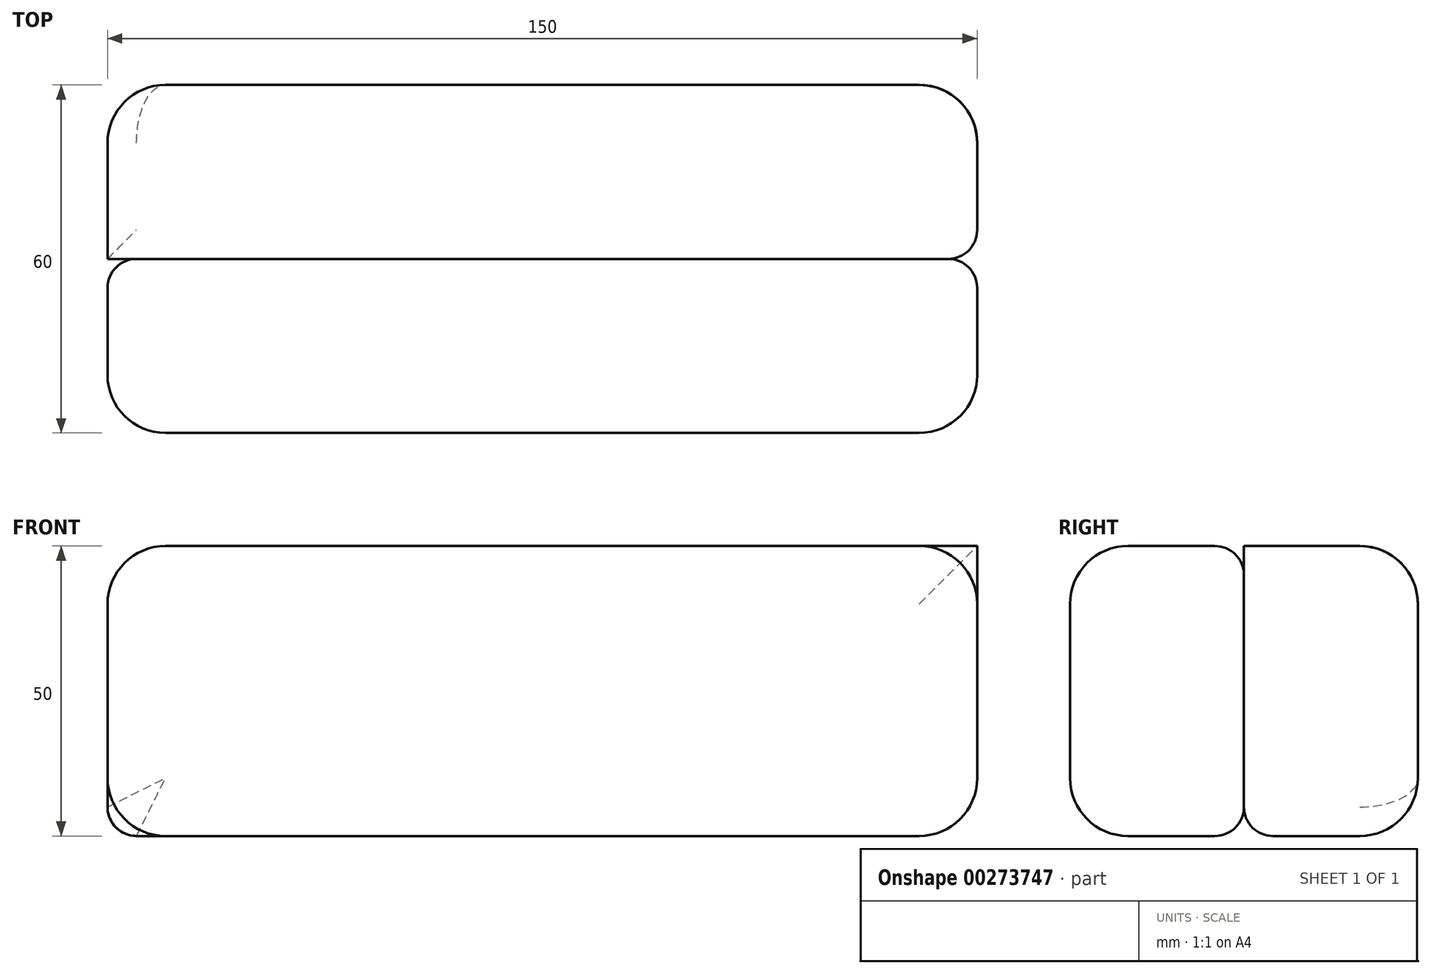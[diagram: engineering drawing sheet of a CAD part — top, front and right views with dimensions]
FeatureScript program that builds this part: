
annotation { "Feature Type Name" : "Feature", "Feature Type Description" : "" }
export const myFeature = defineFeature(function(context is Context, id is Id, definition is map)
    precondition{}
    {
        {
            var Q0;
            Q0=qCreatedBy(makeId("Front.planeOp"),FACE);
            var sketch = newSketch(context, id + "F0", { "sketchPlane" : qUnion([Q0])});
            skLineSegment(sketch, "E0", {"start": v(-86.56, 32.78) * mm, "end": v(-86.56, -17.22) * mm});
            skLineSegment(sketch, "E1", {"start": v(-86.56, -17.22) * mm, "end": v(63.44, -17.22) * mm});
            skLineSegment(sketch, "E2", {"start": v(63.44, -17.22) * mm, "end": v(63.44, 32.78) * mm});
            skLineSegment(sketch, "E3", {"start": v(63.44, 32.78) * mm, "end": v(-86.56, 32.78) * mm});
            skSolve(sketch);
        }
        {
            var Q0;
            Q0=makeQuery(id+"F0.imprint","IMPRINT",FACE,{"disambiguationData":[TD([[makeQuery(id+"F0.imprint","IMPRINT",EDGE,{"derivedFrom":sQuery(id+"F0.wireOp",EDGE,"E0")}),1.0]])]});
            extrude(context, id + "F1", {"entities" : qUnion([Q0]), "depth" : 30 * mm});
        }
        {
            var Q0;
            Q0=makeQuery(id+"F1.opExtrude","CAP_EDGE",EDGE,{"disambiguationData":[OSD([sQuery(id+"F0.wireOp",EDGE,"E3")])],"isStart":false});
            var Q1;
            Q1=makeQuery(id+"F1.opExtrude","CAP_EDGE",EDGE,{"disambiguationData":[OSD([sQuery(id+"F0.wireOp",EDGE,"E1")])],"isStart":false});
            fillet(context, id + "F2", {"entities" : qUnion([Q0, Q1]), "radius" : 10 * mm, "tangentPropagation" : true, "allowEdgeOverflow" : false});
        }
        {
            var Q0;
            Q0=makeQuery(id+"F1.opExtrude","CAP_FACE",FACE,{"disambiguationData":[OSD([sQuery(id+"F0.wireOp",EDGE,"E0"),sQuery(id+"F0.wireOp",EDGE,"E1"),sQuery(id+"F0.wireOp",EDGE,"E2"),sQuery(id+"F0.wireOp",EDGE,"E3")])],"isStart":true});
            extrude(context, id + "F3", {"entities" : qUnion([Q0]), "depth" : 30 * mm});
        }
        {
            var Q0;
            Q0=makeQuery(id+"F3.opExtrude","CAP_EDGE",EDGE,{"disambiguationData":[OSD([sQuery(id+"F0.wireOp",EDGE,"E3")])],"isStart":false});
            var Q1;
            Q1=makeQuery(id+"F3.opExtrude","CAP_EDGE",EDGE,{"disambiguationData":[OSD([sQuery(id+"F0.wireOp",EDGE,"E1")])],"isStart":false});
            var Q2;
            {var subQ0=sQuery(id+"F0.wireOp",EDGE,"E2");var subQ1=sQuery(id+"F0.wireOp",EDGE,"E1");Q2=makeQuery(id+"F3.boolean.opBoolean","MERGE",EDGE,{"derivedFrom":[makeQuery(id+"F1.opExtrude","SWEPT_EDGE",EDGE,{"disambiguationData":[OSD([subQ1,subQ0])]}),makeQuery(id+"F3.opExtrude","SWEPT_EDGE",EDGE,{"disambiguationData":[OSD([subQ1,subQ0])]})]});}
            var Q3;
            Q3=makeQuery(id+"F3.opExtrude","CAP_EDGE",EDGE,{"disambiguationData":[OSD([sQuery(id+"F0.wireOp",EDGE,"E2")])],"isStart":false});
            var Q4;
            Q4=makeQuery(id+"F3.opExtrude","CAP_EDGE",EDGE,{"disambiguationData":[OSD([sQuery(id+"F0.wireOp",EDGE,"E0")])],"isStart":false});
            var Q5;
            {var subQ0=sQuery(id+"F0.wireOp",EDGE,"E3");var subQ1=sQuery(id+"F0.wireOp",EDGE,"E0");Q5=makeQuery(id+"F3.boolean.opBoolean","MERGE",EDGE,{"derivedFrom":[makeQuery(id+"F1.opExtrude","SWEPT_EDGE",EDGE,{"disambiguationData":[OSD([subQ1,subQ0])]}),makeQuery(id+"F3.opExtrude","SWEPT_EDGE",EDGE,{"disambiguationData":[OSD([subQ1,subQ0])]})]});}
            fillet(context, id + "F4", {"entities" : qUnion([Q0, Q1, Q2, Q3, Q4, Q5]), "radius" : 10 * mm, "tangentPropagation" : true, "allowEdgeOverflow" : false});
        }
        {
            var Q0;
            {var subQ0=sQuery(id+"F0.wireOp",EDGE,"E3");Q0=makeQuery(id+"F2.opFillet","BLEND_EDGE",EDGE,{"blendedFrom":[makeQuery(id+"F1.opExtrude","CAP_EDGE",EDGE,{"disambiguationData":[OSD([subQ0])],"isStart":false}),makeQuery(id+"F1.opExtrude","CAP_FACE",FACE,{"disambiguationData":[OSD([sQuery(id+"F0.wireOp",EDGE,"E0"),sQuery(id+"F0.wireOp",EDGE,"E1"),sQuery(id+"F0.wireOp",EDGE,"E2"),subQ0])],"isStart":false})],"blendedInto":[makeQuery(id+"F1.opExtrude","CAP_FACE",FACE,{"disambiguationData":[OSD([sQuery(id+"F0.wireOp",EDGE,"E0"),sQuery(id+"F0.wireOp",EDGE,"E1"),sQuery(id+"F0.wireOp",EDGE,"E2"),subQ0])],"isStart":false})]});}
            var Q1;
            {var subQ0=sQuery(id+"F0.wireOp",EDGE,"E0");Q1=makeQuery(id+"F4.opFillet","BLEND_EDGE",EDGE,{"blendedFrom":[makeQuery(id+"F1.opExtrude","CAP_EDGE",EDGE,{"disambiguationData":[OSD([subQ0])],"isStart":false}),makeQuery(id+"F2.opFillet","BLEND_EDGE",EDGE,{"blendedFrom":[makeQuery(id+"F1.opExtrude","CAP_EDGE",EDGE,{"disambiguationData":[OSD([sQuery(id+"F0.wireOp",EDGE,"E1")])],"isStart":false}),makeQuery(id+"F1.opExtrude","SWEPT_FACE",FACE,{"disambiguationData":[OSD([subQ0])]})],"blendedInto":[makeQuery(id+"F1.opExtrude","SWEPT_FACE",FACE,{"disambiguationData":[OSD([subQ0])]})]})],"blendedInto":[]});}
            var Q2;
            {var subQ0=sQuery(id+"F0.wireOp",EDGE,"E0");var subQ1=sQuery(id+"F0.wireOp",EDGE,"E1");Q2=makeQuery(id+"F4.opFillet","BLEND_FACE",FACE,{"disambiguationData":[OSD([subQ0,subQ1]),TDD([makeQuery(id+"F2.opFillet","BLEND_EDGE",EDGE,{"blendedFrom":[makeQuery(id+"F1.opExtrude","CAP_EDGE",EDGE,{"disambiguationData":[OSD([subQ1])],"isStart":false}),makeQuery(id+"F1.opExtrude","SWEPT_FACE",FACE,{"disambiguationData":[OSD([subQ0])]})],"blendedInto":[makeQuery(id+"F1.opExtrude","SWEPT_FACE",FACE,{"disambiguationData":[OSD([subQ0])]})]})])]});}
            var Q3;
            Q3=makeQuery(id+"F1.opExtrude","CAP_FACE",FACE,{"disambiguationData":[OSD([sQuery(id+"F0.wireOp",EDGE,"E0"),sQuery(id+"F0.wireOp",EDGE,"E1"),sQuery(id+"F0.wireOp",EDGE,"E2"),sQuery(id+"F0.wireOp",EDGE,"E3")])],"isStart":false});
            var Q4;
            {var subQ0=sQuery(id+"F0.wireOp",EDGE,"E1");var subQ1=sQuery(id+"F0.wireOp",EDGE,"E0");Q4=makeQuery(id+"F4.opFillet","BLEND_FACE",FACE,{"disambiguationData":[OSD([subQ1,subQ0]),TDD([makeQuery(id+"F3.boolean.opBoolean","MERGE",EDGE,{"derivedFrom":[makeQuery(id+"F1.opExtrude","SWEPT_EDGE",EDGE,{"disambiguationData":[OSD([subQ1,subQ0])]}),makeQuery(id+"F3.opExtrude","SWEPT_EDGE",EDGE,{"disambiguationData":[OSD([subQ1,subQ0])]})]})])]});}
            var Q5;
            {var subQ0=sQuery(id+"F0.wireOp",EDGE,"E0");Q5=makeQuery(id+"F4.opFillet","BLEND_FACE",FACE,{"disambiguationData":[OSD([subQ0]),TDD([makeQuery(id+"F1.opExtrude","CAP_EDGE",EDGE,{"disambiguationData":[OSD([subQ0])],"isStart":false})])]});}
            var Q6;
            {var subQ0=sQuery(id+"F0.wireOp",EDGE,"E1");var subQ1=sQuery(id+"F0.wireOp",EDGE,"E0");Q6=makeQuery(id+"F4.opFillet","BLEND_EDGE",EDGE,{"blendedFrom":[makeQuery(id+"F2.opFillet","BLEND_EDGE",EDGE,{"blendedFrom":[makeQuery(id+"F1.opExtrude","CAP_EDGE",EDGE,{"disambiguationData":[OSD([subQ0])],"isStart":false}),makeQuery(id+"F1.opExtrude","SWEPT_FACE",FACE,{"disambiguationData":[OSD([subQ1])]})],"blendedInto":[makeQuery(id+"F1.opExtrude","SWEPT_FACE",FACE,{"disambiguationData":[OSD([subQ1])]})]}),makeQuery(id+"F3.boolean.opBoolean","MERGE",EDGE,{"derivedFrom":[makeQuery(id+"F1.opExtrude","SWEPT_EDGE",EDGE,{"disambiguationData":[OSD([subQ1,subQ0])]}),makeQuery(id+"F3.opExtrude","SWEPT_EDGE",EDGE,{"disambiguationData":[OSD([subQ1,subQ0])]})]})],"blendedInto":[]});}
            var Q7;
            {var subQ0=sQuery(id+"F0.wireOp",EDGE,"E1");Q7=makeQuery(id+"F2.opFillet","BLEND_EDGE",EDGE,{"blendedFrom":[makeQuery(id+"F1.opExtrude","CAP_EDGE",EDGE,{"disambiguationData":[OSD([subQ0])],"isStart":false}),makeQuery(id+"F1.opExtrude","CAP_FACE",FACE,{"disambiguationData":[OSD([sQuery(id+"F0.wireOp",EDGE,"E0"),subQ0,sQuery(id+"F0.wireOp",EDGE,"E2"),sQuery(id+"F0.wireOp",EDGE,"E3")])],"isStart":false})],"blendedInto":[makeQuery(id+"F1.opExtrude","CAP_FACE",FACE,{"disambiguationData":[OSD([sQuery(id+"F0.wireOp",EDGE,"E0"),subQ0,sQuery(id+"F0.wireOp",EDGE,"E2"),sQuery(id+"F0.wireOp",EDGE,"E3")])],"isStart":false})]});}
            var Q8;
            Q8=makeQuery(id+"F2.opFillet","BLEND_FACE",FACE,{"disambiguationData":[OSD([sQuery(id+"F0.wireOp",EDGE,"E1")])]});
            var Q9;
            {var subQ0=sQuery(id+"F0.wireOp",EDGE,"E1");Q9=makeQuery(id+"F3.boolean.opBoolean","MERGE",FACE,{"derivedFrom":[makeQuery(id+"F1.opExtrude","SWEPT_FACE",FACE,{"disambiguationData":[OSD([subQ0])]}),makeQuery(id+"F3.opExtrude","SWEPT_FACE",FACE,{"disambiguationData":[OSD([subQ0])]})]});}
            var Q10;
            {var subQ0=sQuery(id+"F0.wireOp",EDGE,"E1");var subQ1=sQuery(id+"F0.wireOp",EDGE,"E0");Q10=makeQuery(id+"F4.opFillet","BLEND_EDGE",EDGE,{"blendedFrom":[makeQuery(id+"F3.boolean.opBoolean","MERGE",EDGE,{"derivedFrom":[makeQuery(id+"F1.opExtrude","SWEPT_EDGE",EDGE,{"disambiguationData":[OSD([subQ1,subQ0])]}),makeQuery(id+"F3.opExtrude","SWEPT_EDGE",EDGE,{"disambiguationData":[OSD([subQ1,subQ0])]})]}),makeQuery(id+"F3.boolean.opBoolean","MERGE",FACE,{"derivedFrom":[makeQuery(id+"F1.opExtrude","SWEPT_FACE",FACE,{"disambiguationData":[OSD([subQ0])]}),makeQuery(id+"F3.opExtrude","SWEPT_FACE",FACE,{"disambiguationData":[OSD([subQ0])]})]})],"blendedInto":[makeQuery(id+"F3.boolean.opBoolean","MERGE",FACE,{"derivedFrom":[makeQuery(id+"F1.opExtrude","SWEPT_FACE",FACE,{"disambiguationData":[OSD([subQ0])]}),makeQuery(id+"F3.opExtrude","SWEPT_FACE",FACE,{"disambiguationData":[OSD([subQ0])]})]})]});}
            var Q11;
            {var subQ0=sQuery(id+"F0.wireOp",EDGE,"E0");Q11=makeQuery(id+"F4.opFillet","BLEND_EDGE",EDGE,{"blendedFrom":[makeQuery(id+"F1.opExtrude","CAP_EDGE",EDGE,{"disambiguationData":[OSD([subQ0])],"isStart":false}),makeQuery(id+"F1.opExtrude","CAP_FACE",FACE,{"disambiguationData":[OSD([subQ0,sQuery(id+"F0.wireOp",EDGE,"E1"),sQuery(id+"F0.wireOp",EDGE,"E2"),sQuery(id+"F0.wireOp",EDGE,"E3")])],"isStart":false})],"blendedInto":[makeQuery(id+"F1.opExtrude","CAP_FACE",FACE,{"disambiguationData":[OSD([subQ0,sQuery(id+"F0.wireOp",EDGE,"E1"),sQuery(id+"F0.wireOp",EDGE,"E2"),sQuery(id+"F0.wireOp",EDGE,"E3")])],"isStart":false})]});}
            var Q12;
            {var subQ0=sQuery(id+"F0.wireOp",EDGE,"E1");Q12=makeQuery(id+"F4.opFillet","BLEND_EDGE",EDGE,{"blendedFrom":[makeQuery(id+"F2.opFillet","BLEND_EDGE",EDGE,{"blendedFrom":[makeQuery(id+"F1.opExtrude","CAP_EDGE",EDGE,{"disambiguationData":[OSD([subQ0])],"isStart":false}),makeQuery(id+"F1.opExtrude","SWEPT_FACE",FACE,{"disambiguationData":[OSD([sQuery(id+"F0.wireOp",EDGE,"E0")])]})],"blendedInto":[makeQuery(id+"F1.opExtrude","SWEPT_FACE",FACE,{"disambiguationData":[OSD([sQuery(id+"F0.wireOp",EDGE,"E0")])]})]}),makeQuery(id+"F2.opFillet","BLEND_FACE",FACE,{"disambiguationData":[OSD([subQ0])]})],"blendedInto":[makeQuery(id+"F2.opFillet","BLEND_FACE",FACE,{"disambiguationData":[OSD([subQ0])]})]});}
            var Q13;
            Q13=makeQuery(id+"F4.opFillet","BLEND_FACE",FACE,{"disambiguationData":[OSD([sQuery(id+"F0.wireOp",EDGE,"E1")])]});
            var Q14;
            {var subQ0=sQuery(id+"F0.wireOp",EDGE,"E1");Q14=makeQuery(id+"F4.opFillet","BLEND_EDGE",EDGE,{"blendedFrom":[makeQuery(id+"F3.opExtrude","CAP_EDGE",EDGE,{"disambiguationData":[OSD([subQ0])],"isStart":false}),makeQuery(id+"F3.boolean.opBoolean","MERGE",FACE,{"derivedFrom":[makeQuery(id+"F1.opExtrude","SWEPT_FACE",FACE,{"disambiguationData":[OSD([subQ0])]}),makeQuery(id+"F3.opExtrude","SWEPT_FACE",FACE,{"disambiguationData":[OSD([subQ0])]})]})],"blendedInto":[makeQuery(id+"F3.boolean.opBoolean","MERGE",FACE,{"derivedFrom":[makeQuery(id+"F1.opExtrude","SWEPT_FACE",FACE,{"disambiguationData":[OSD([subQ0])]}),makeQuery(id+"F3.opExtrude","SWEPT_FACE",FACE,{"disambiguationData":[OSD([subQ0])]})]})]});}
            fillet(context, id + "F5", {"entities" : qUnion([Q0, Q1, Q2, Q3, Q4, Q5, Q6, Q7, Q8, Q9, Q10, Q11, Q12, Q13, Q14]), "radius" : 5 * mm, "tangentPropagation" : true, "allowEdgeOverflow" : false});
        }
    });
